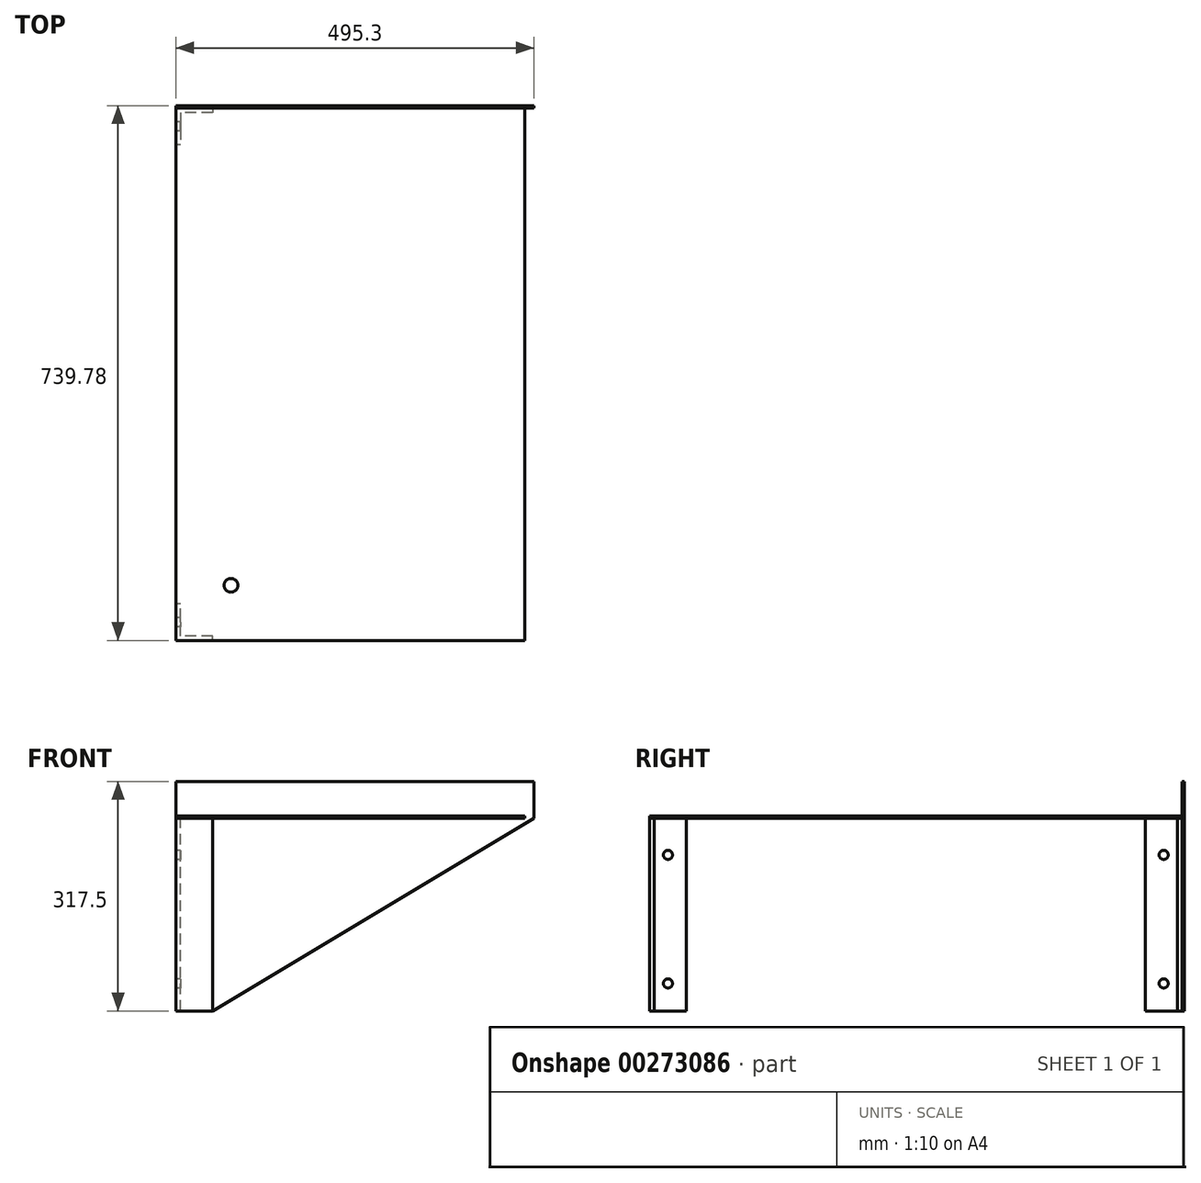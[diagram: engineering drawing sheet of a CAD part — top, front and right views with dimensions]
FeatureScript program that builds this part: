
annotation { "Feature Type Name" : "Feature", "Feature Type Description" : "" }
export const myFeature = defineFeature(function(context is Context, id is Id, definition is map)
    precondition{}
    {
        {
            var Q0;
            Q0=qCreatedBy(makeId("Top.planeOp"),FACE);
            var sketch = newSketch(context, id + "F0", { "sketchPlane" : qUnion([Q0])});
            skLineSegment(sketch, "E0.bottom", {"start": v(241.3, -368.3) * mm, "end": v(-241.3, -368.3) * mm});
            skLineSegment(sketch, "E0.top", {"start": v(241.3, 368.3) * mm, "end": v(-241.3, 368.3) * mm});
            skLineSegment(sketch, "E0.left", {"start": v(241.3, -368.3) * mm, "end": v(241.3, 368.3) * mm});
            skLineSegment(sketch, "E0.right", {"start": v(-241.3, -368.3) * mm, "end": v(-241.3, 368.3) * mm});
            skPoint(sketch, "E0.middle", {"position": v(0, 0) * mm});
            skCircle(sketch, "E1", {"center": v(-165.1, -292.1) * mm, "radius": 9.52 * mm});
            skSolve(sketch);
        }
        {
            var Q0;
            Q0 = qSketchRegion(id + "F0", true);
            extrude(context, id + "F1", {"entities" : qUnion([Q0]), "depth" : 3.17 * mm});
        }
        {
            var Q0;
            Q0=makeQuery(id+"F1.opExtrude","CAP_FACE",FACE,{"disambiguationData":[OSD([sQuery(id+"F0.wireOp",EDGE,"E0.bottom"),sQuery(id+"F0.wireOp",EDGE,"E0.top"),sQuery(id+"F0.wireOp",EDGE,"E0.left"),sQuery(id+"F0.wireOp",EDGE,"E0.right"),sQuery(id+"F0.wireOp",EDGE,"E1")])],"isStart":true});
            var sketch = newSketch(context, id + "F2", { "sketchPlane" : qUnion([Q0])});
            skLineSegment(sketch, "E2", {"start": v(-241.3, -368.3) * mm, "end": v(-190.5, -368.3) * mm});
            skLineSegment(sketch, "E3", {"start": v(-190.5, -368.3) * mm, "end": v(-190.5, -361.95) * mm});
            skLineSegment(sketch, "E4", {"start": v(-190.5, -361.95) * mm, "end": v(-234.95, -361.95) * mm});
            skLineSegment(sketch, "E5", {"start": v(-234.95, -361.95) * mm, "end": v(-234.95, -317.5) * mm});
            skLineSegment(sketch, "E6", {"start": v(-234.95, -317.5) * mm, "end": v(-241.3, -317.5) * mm});
            skLineSegment(sketch, "E7", {"start": v(-241.3, -317.5) * mm, "end": v(-241.3, -368.3) * mm});
            skLineSegment(sketch, "E8", {"start": v(-241.3, 368.3) * mm, "end": v(-190.5, 368.3) * mm});
            skLineSegment(sketch, "E9", {"start": v(-190.5, 368.3) * mm, "end": v(-190.5, 361.95) * mm});
            skLineSegment(sketch, "E10", {"start": v(-190.5, 361.95) * mm, "end": v(-234.95, 361.95) * mm});
            skLineSegment(sketch, "E11", {"start": v(-234.95, 361.95) * mm, "end": v(-234.95, 317.5) * mm});
            skLineSegment(sketch, "E12", {"start": v(-234.95, 317.5) * mm, "end": v(-241.3, 317.5) * mm});
            skLineSegment(sketch, "E13", {"start": v(-241.3, 317.5) * mm, "end": v(-241.3, 368.3) * mm});
            skSolve(sketch);
        }
        {
            var Q0;
            Q0 = qSketchRegion(id + "F2", true);
            extrude(context, id + "F3", {"entities" : qUnion([Q0]), "depth" : 266.7 * mm});
        }
        {
            var Q0;
            Q0=makeQuery(id+"F3.opExtrude","SWEPT_FACE",FACE,{"disambiguationData":[OSD([sQuery(id+"F2.wireOp",EDGE,"E2")])]});
            var sketch = newSketch(context, id + "F4", { "sketchPlane" : qUnion([Q0])});
            skLineSegment(sketch, "E14", {"start": v(241.3, -266.7) * mm, "end": v(190.5, -266.7) * mm});
            skLineSegment(sketch, "E15", {"start": v(190.5, -266.7) * mm, "end": v(-254, 0) * mm});
            skLineSegment(sketch, "E16", {"start": v(-254, 0) * mm, "end": v(-254, 50.8) * mm});
            skLineSegment(sketch, "E17", {"start": v(-254, 50.8) * mm, "end": v(241.3, 50.8) * mm});
            skLineSegment(sketch, "E18", {"start": v(241.3, 50.8) * mm, "end": v(241.3, -266.7) * mm});
            skSolve(sketch);
        }
        {
            var Q0;
            Q0 = qSketchRegion(id + "F4", true);
            extrude(context, id + "F5", {"entities" : qUnion([Q0]), "depth" : 3.17 * mm});
        }
        {
            var Q0;
            Q0=makeQuery(id+"F3.opExtrude","SWEPT_FACE",FACE,{"disambiguationData":[OSD([sQuery(id+"F2.wireOp",EDGE,"E7")])]});
            var sketch = newSketch(context, id + "F6", { "sketchPlane" : qUnion([Q0])});
            skCircle(sketch, "E19", {"center": v(-342.9, -50.8) * mm, "radius": 6.35 * mm});
            skCircle(sketch, "E20", {"center": v(-342.9, -228.6) * mm, "radius": 6.35 * mm});
            skCircle(sketch, "E21", {"center": v(342.9, -228.6) * mm, "radius": 6.35 * mm});
            skCircle(sketch, "E22", {"center": v(342.9, -50.8) * mm, "radius": 6.35 * mm});
            skSolve(sketch);
        }
        {
            var Q0;
            Q0 = qSketchRegion(id + "F6", true);
            extrude(context, id + "F7", {"entities" : qUnion([Q0]), "operationType" : NewBodyOperationType.REMOVE, "oppositeDirection" : true, "depth" : 25.4 * mm});
        }
    });
